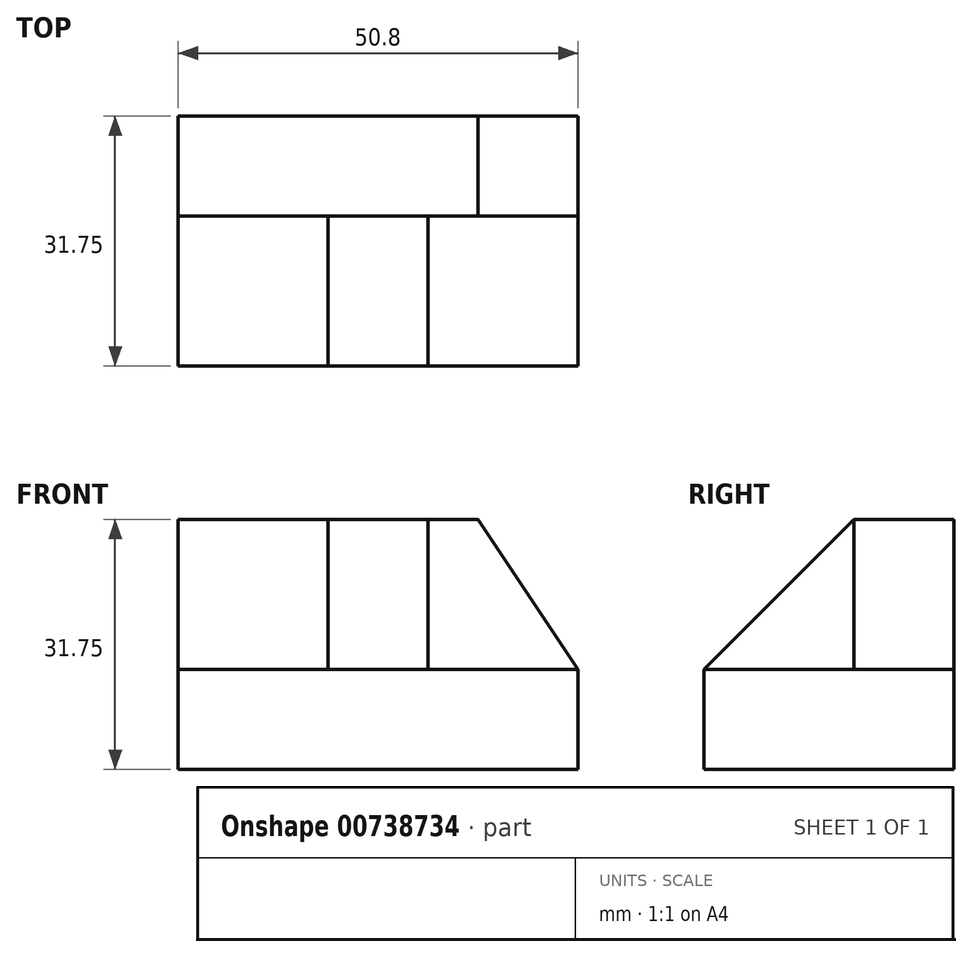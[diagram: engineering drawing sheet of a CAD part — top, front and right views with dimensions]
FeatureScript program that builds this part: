
annotation { "Feature Type Name" : "Feature", "Feature Type Description" : "" }
export const myFeature = defineFeature(function(context is Context, id is Id, definition is map)
    precondition{}
    {
        {
            var Q0;
            Q0=qCreatedBy(makeId("Front.planeOp"),FACE);
            var sketch = newSketch(context, id + "F0", { "sketchPlane" : qUnion([Q0])});
            skLineSegment(sketch, "E0", {"start": v(0, 0) * mm, "end": v(50.8, 0) * mm});
            skLineSegment(sketch, "E1", {"start": v(50.8, 0) * mm, "end": v(50.8, 31.75) * mm});
            skLineSegment(sketch, "E2", {"start": v(50.8, 31.75) * mm, "end": v(0, 31.75) * mm});
            skLineSegment(sketch, "E3", {"start": v(0, 31.75) * mm, "end": v(0, 0) * mm});
            skSolve(sketch);
        }
        {
            var Q0;
            Q0 = qSketchRegion(id + "F0", true);
            extrude(context, id + "F1", {"entities" : qUnion([Q0]), "depth" : 31.75 * mm, "offsetDistance" : 25.4 * mm});
        }
        {
            var Q0;
            Q0=makeQuery(id+"F1.opExtrude","CAP_FACE",FACE,{"disambiguationData":[OSD([sQuery(id+"F0.wireOp",EDGE,"E0"),sQuery(id+"F0.wireOp",EDGE,"E1"),sQuery(id+"F0.wireOp",EDGE,"E2"),sQuery(id+"F0.wireOp",EDGE,"E3")])],"isStart":false});
            var sketch = newSketch(context, id + "F2", { "sketchPlane" : qUnion([Q0])});
            skLineSegment(sketch, "E4", {"start": v(0, 31.75) * mm, "end": v(19.05, 31.75) * mm});
            skLineSegment(sketch, "E5", {"start": v(19.05, 31.75) * mm, "end": v(19.05, 12.7) * mm});
            skLineSegment(sketch, "E6", {"start": v(19.05, 12.7) * mm, "end": v(0, 12.7) * mm});
            skLineSegment(sketch, "E7", {"start": v(0, 12.7) * mm, "end": v(0, 31.75) * mm});
            skLineSegment(sketch, "E8", {"start": v(50.8, 31.75) * mm, "end": v(50.8, 12.7) * mm});
            skLineSegment(sketch, "E9", {"start": v(50.8, 12.7) * mm, "end": v(31.75, 12.7) * mm});
            skLineSegment(sketch, "E10", {"start": v(31.75, 12.7) * mm, "end": v(31.75, 31.75) * mm});
            skLineSegment(sketch, "E11", {"start": v(31.75, 31.75) * mm, "end": v(50.8, 31.75) * mm});
            skSolve(sketch);
        }
        {
            var Q0;
            Q0 = qSketchRegion(id + "F2", true);
            extrude(context, id + "F3", {"entities" : qUnion([Q0]), "operationType" : NewBodyOperationType.REMOVE, "oppositeDirection" : true, "depth" : 19.05 * mm, "offsetDistance" : 25.4 * mm});
        }
        {
            var Q0;
            Q0=makeQuery(id+"F3.boolean.opBoolean","COPY",FACE,{"derivedFrom":makeQuery(id+"F3.opExtrude","CAP_FACE",FACE,{"disambiguationData":[OSD([sQuery(id+"F2.wireOp",EDGE,"E8"),sQuery(id+"F2.wireOp",EDGE,"E9"),sQuery(id+"F2.wireOp",EDGE,"E10"),sQuery(id+"F2.wireOp",EDGE,"E11")])],"isStart":false})});
            var sketch = newSketch(context, id + "F4", { "sketchPlane" : qUnion([Q0])});
            skLineSegment(sketch, "E12", {"start": v(50.8, 12.7) * mm, "end": v(38.1, 31.75) * mm});
            skLineSegment(sketch, "E13", {"start": v(38.1, 31.75) * mm, "end": v(50.8, 31.75) * mm});
            skLineSegment(sketch, "E14", {"start": v(50.8, 31.75) * mm, "end": v(50.8, 12.7) * mm});
            skSolve(sketch);
        }
        {
            var Q0;
            Q0 = qSketchRegion(id + "F4", true);
            extrude(context, id + "F5", {"entities" : qUnion([Q0]), "operationType" : NewBodyOperationType.REMOVE, "oppositeDirection" : true, "depth" : 25.4 * mm, "offsetDistance" : 25.4 * mm});
        }
        {
            var Q0;
            Q0=makeQuery(id+"F3.boolean.opBoolean","COPY",FACE,{"derivedFrom":makeQuery(id+"F3.opExtrude","SWEPT_FACE",FACE,{"disambiguationData":[OSD([sQuery(id+"F2.wireOp",EDGE,"E10")])]})});
            var sketch = newSketch(context, id + "F6", { "sketchPlane" : qUnion([Q0])});
            skLineSegment(sketch, "E15", {"start": v(-31.75, 12.7) * mm, "end": v(-12.7, 31.75) * mm});
            skLineSegment(sketch, "E16", {"start": v(-12.7, 31.75) * mm, "end": v(-31.75, 31.75) * mm});
            skLineSegment(sketch, "E17", {"start": v(-31.75, 31.75) * mm, "end": v(-31.75, 12.7) * mm});
            skSolve(sketch);
        }
        {
            var Q0;
            Q0=makeQuery(id+"F6.imprint","IMPRINT",FACE,{"disambiguationData":[TD([[makeQuery(id+"F6.imprint","IMPRINT",EDGE,{"derivedFrom":sQuery(id+"F6.wireOp",EDGE,"E15")}),1.0]])]});
            extrude(context, id + "F7", {"entities" : qUnion([Q0]), "operationType" : NewBodyOperationType.REMOVE, "endBound" : BoundingType.THROUGH_ALL, "oppositeDirection" : true, "depth" : 25.4 * mm, "offsetDistance" : 25.4 * mm});
        }
    });
